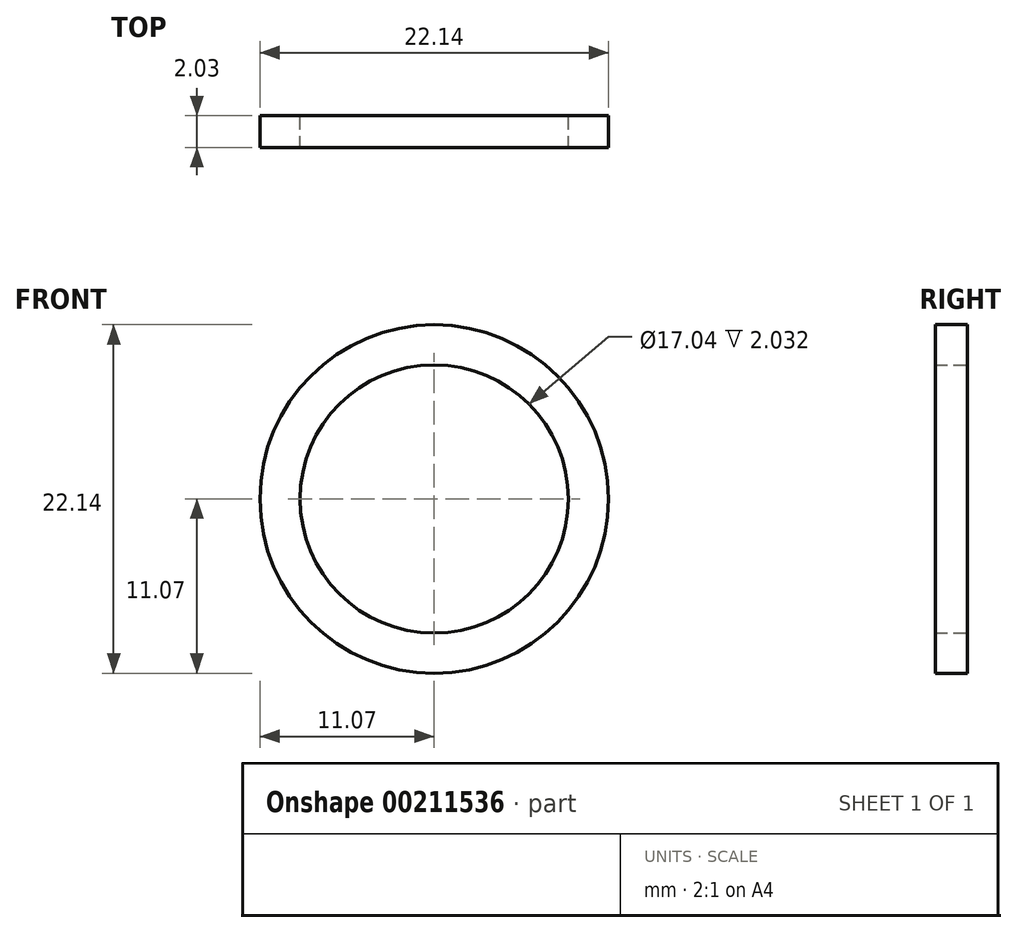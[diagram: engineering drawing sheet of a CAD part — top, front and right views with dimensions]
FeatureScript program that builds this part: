
annotation { "Feature Type Name" : "Feature", "Feature Type Description" : "" }
export const myFeature = defineFeature(function(context is Context, id is Id, definition is map)
    precondition{}
    {
        {
            var Q0;
            Q0=qCreatedBy(makeId("Front.planeOp"),FACE);
            var sketch = newSketch(context, id + "F0", { "sketchPlane" : qUnion([Q0])});
            skCircle(sketch, "E0", {"center": v(0, 0) * mm, "radius": 11.07 * mm});
            skCircle(sketch, "E1", {"center": v(0, 0) * mm, "radius": 8.52 * mm});
            skSolve(sketch);
        }
        {
            var Q0;
            Q0 = qSketchRegion(id + "F0", true);
            extrude(context, id + "F1", {"entities" : qUnion([Q0]), "depth" : 2.03 * mm});
        }
    });
